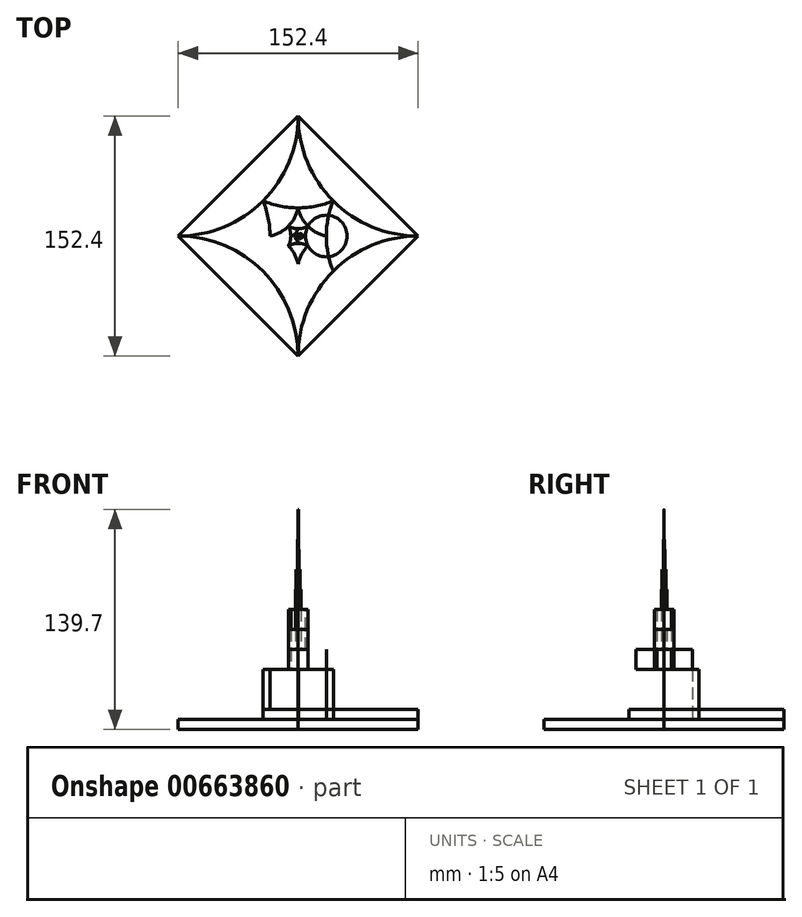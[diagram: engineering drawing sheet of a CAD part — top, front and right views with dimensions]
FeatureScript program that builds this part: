
annotation { "Feature Type Name" : "Feature", "Feature Type Description" : "" }
export const myFeature = defineFeature(function(context is Context, id is Id, definition is map)
    precondition{}
    {
        {
            var Q0;
            Q0=qCreatedBy(makeId("Top.planeOp"),FACE);
            var sketch = newSketch(context, id + "F0", { "sketchPlane" : qUnion([Q0])});
            skLineSegment(sketch, "E0", {"start": v(0, 76.2) * mm, "end": v(-76.2, 0) * mm});
            skLineSegment(sketch, "E1", {"start": v(-76.2, 0) * mm, "end": v(0, -76.2) * mm});
            skLineSegment(sketch, "E2", {"start": v(0, -76.2) * mm, "end": v(76.2, 0) * mm});
            skLineSegment(sketch, "E3", {"start": v(76.2, 0) * mm, "end": v(0, 76.2) * mm});
            skArc(sketch, "E4", {"start": v(-76.2, 0) * mm, "mid": v(-22.32, 22.32) * mm, "end": v(0, 76.2) * mm});
            skArc(sketch, "E5", {"start": v(76.2, 0) * mm, "mid": v(22.35, 22.28) * mm, "end": v(0, 76.1) * mm});
            skArc(sketch, "E6", {"start": v(-76.2, 0) * mm, "mid": v(-22.32, -22.32) * mm, "end": v(0, -76.2) * mm});
            skArc(sketch, "E7", {"start": v(0, -76.2) * mm, "mid": v(22.32, -22.32) * mm, "end": v(76.2, 0) * mm});
            skArc(sketch, "E8", {"start": v(-22.32, 22.32) * mm, "mid": v(0, 17.88) * mm, "end": v(22.32, 22.32) * mm});
            skArc(sketch, "E9", {"start": v(-22.32, -22.32) * mm, "mid": v(0, -17.88) * mm, "end": v(22.32, -22.32) * mm});
            skArc(sketch, "E10", {"start": v(22.32, 22.32) * mm, "mid": v(17.88, 0) * mm, "end": v(22.32, -22.32) * mm});
            skArc(sketch, "E11", {"start": v(-22.32, 22.32) * mm, "mid": v(-17.88, 0) * mm, "end": v(-22.32, -22.32) * mm});
            skArc(sketch, "E12", {"start": v(-17.88, 0) * mm, "mid": v(-6.23, -6.23) * mm, "end": v(0, -17.88) * mm});
            skArc(sketch, "E13", {"start": v(0, -17.88) * mm, "mid": v(6.23, -6.23) * mm, "end": v(17.88, 0) * mm});
            skArc(sketch, "E14", {"start": v(-17.88, 0) * mm, "mid": v(-6.23, 6.23) * mm, "end": v(0, 17.88) * mm});
            skArc(sketch, "E15", {"start": v(0, 17.88) * mm, "mid": v(6.23, 6.23) * mm, "end": v(17.88, 0) * mm});
            skArc(sketch, "E16", {"start": v(-6.23, 6.23) * mm, "mid": v(0, 4.67) * mm, "end": v(6.23, 6.23) * mm});
            skArc(sketch, "E17", {"start": v(-6.23, 6.23) * mm, "mid": v(-4.67, 0) * mm, "end": v(-6.23, -6.23) * mm});
            skArc(sketch, "E18", {"start": v(-6.23, -6.23) * mm, "mid": v(0, -4.67) * mm, "end": v(6.23, -6.23) * mm});
            skArc(sketch, "E19", {"start": v(6.23, 6.23) * mm, "mid": v(4.67, 0) * mm, "end": v(6.23, -6.23) * mm});
            skArc(sketch, "E20", {"start": v(0, 4.67) * mm, "mid": v(1.69, 1.69) * mm, "end": v(4.67, 0) * mm});
            skArc(sketch, "E21", {"start": v(4.67, 0) * mm, "mid": v(1.69, -1.69) * mm, "end": v(0, -4.67) * mm});
            skArc(sketch, "E22", {"start": v(0, -4.67) * mm, "mid": v(-1.69, -1.69) * mm, "end": v(-4.67, 0) * mm});
            skArc(sketch, "E23", {"start": v(0, 4.67) * mm, "mid": v(-1.69, 1.69) * mm, "end": v(-4.67, 0) * mm});
            skArc(sketch, "E24", {"start": v(1.69, 1.69) * mm, "mid": v(0, 1.24) * mm, "end": v(-1.69, 1.69) * mm});
            skArc(sketch, "E25", {"start": v(-1.69, 1.69) * mm, "mid": v(-1.24, 0) * mm, "end": v(-1.69, -1.69) * mm});
            skArc(sketch, "E26", {"start": v(-1.69, -1.69) * mm, "mid": v(0, -1.24) * mm, "end": v(1.69, -1.69) * mm});
            skArc(sketch, "E27", {"start": v(1.69, -1.69) * mm, "mid": v(1.24, 0) * mm, "end": v(1.69, 1.7) * mm});
            skArc(sketch, "E28", {"start": v(0, 1.24) * mm, "mid": v(0.45, 0.45) * mm, "end": v(1.24, 0) * mm});
            skArc(sketch, "E29", {"start": v(1.24, 0) * mm, "mid": v(0.45, -0.45) * mm, "end": v(0, -1.24) * mm});
            skArc(sketch, "E30", {"start": v(0, -1.24) * mm, "mid": v(-0.45, -0.45) * mm, "end": v(-1.24, 0) * mm});
            skArc(sketch, "E31", {"start": v(0, 1.24) * mm, "mid": v(-0.45, 0.45) * mm, "end": v(-1.24, 0) * mm});
            skArc(sketch, "E32", {"start": v(-0.45, 0.45) * mm, "mid": v(0, 0.33) * mm, "end": v(0.45, 0.45) * mm});
            skArc(sketch, "E33", {"start": v(0.45, 0.45) * mm, "mid": v(0.33, 0) * mm, "end": v(0.45, -0.45) * mm});
            skArc(sketch, "E34", {"start": v(0.45, -0.45) * mm, "mid": v(0, -0.33) * mm, "end": v(-0.45, -0.45) * mm});
            skArc(sketch, "E35", {"start": v(-0.45, 0.45) * mm, "mid": v(-0.33, 0) * mm, "end": v(-0.45, -0.45) * mm});
            skArc(sketch, "E36", {"start": v(0, 0.33) * mm, "mid": v(-0.12, 0.12) * mm, "end": v(-0.33, 0) * mm});
            skArc(sketch, "E37", {"start": v(0, 0.33) * mm, "mid": v(0.12, 0.12) * mm, "end": v(0.33, 0) * mm});
            skArc(sketch, "E38", {"start": v(0.33, 0) * mm, "mid": v(0.12, -0.12) * mm, "end": v(0, -0.33) * mm});
            skArc(sketch, "E39", {"start": v(-0.33, 0) * mm, "mid": v(-0.12, -0.12) * mm, "end": v(0, -0.33) * mm});
            skArc(sketch, "E40", {"start": v(0.12, -0.12) * mm, "mid": v(0, -0.09) * mm, "end": v(-0.12, -0.12) * mm});
            skArc(sketch, "E41", {"start": v(-0.12, -0.12) * mm, "mid": v(-0.09, 0) * mm, "end": v(-0.12, 0.12) * mm});
            skArc(sketch, "E42", {"start": v(-0.12, 0.12) * mm, "mid": v(0, 0.09) * mm, "end": v(0.12, 0.12) * mm});
            skArc(sketch, "E43", {"start": v(0.12, 0.12) * mm, "mid": v(0.1, 0) * mm, "end": v(0.12, -0.12) * mm});
            skCircle(sketch, "E44", {"center": v(0, 0) * mm, "radius": 0.09 * mm});
            skSolve(sketch);
        }
        {
            var Q0;
            {var subQ1=sQuery(id+"F0.wireOp",EDGE,"E5");var subQ3=sQuery(id+"F0.wireOp",EDGE,"kofghPFV-T25e-cAOz-wG0u-t3LKG4Hneenn");var subQ4=makeQuery(id+"F0.imprint","INTERSECT",VERTEX,{"derivedFrom":[subQ1,subQ3,sQuery(id+"F0.wireOp",EDGE,"4kuBeRdD-5hCW-bFI1-FARk-7CcU9GoLoFz7")]});Q0=makeQuery(id+"F0.imprint","IMPRINT",FACE,{"disambiguationData":[TD([[makeQuery(id+"F0.imprint","IMPRINT",EDGE,{"disambiguationData":[TD([[subQ4,-1.0]])],"derivedFrom":subQ3}),1.0]])]});}
            var Q1;
            {var subQ0=sQuery(id+"F0.wireOp",EDGE,"E5");var subQ1=sQuery(id+"F0.wireOp",EDGE,"E4");var subQ2=makeQuery(id+"F0.imprint","INTERSECT",VERTEX,{"derivedFrom":[subQ1,subQ0]});Q1=makeQuery(id+"F0.imprint","IMPRINT",FACE,{"disambiguationData":[TD([[makeQuery(id+"F0.imprint","IMPRINT",EDGE,{"disambiguationData":[TD([[subQ2,1.0]])],"derivedFrom":subQ1}),-1.0]])]});}
            var Q2;
            {var subQ3=sQuery(id+"F0.wireOp",EDGE,"0P1LDTDX-IqJU-1oAK-Dlat-AA7q8Yj1gsRT");var subQ6=makeQuery(id+"F0.imprint","INTERSECT",VERTEX,{"derivedFrom":[subQ3,sQuery(id+"F0.wireOp",EDGE,"TcEtzozo-cGTj-XFDn-72LJ-OHSNKTu2x1DY")]});Q2=makeQuery(id+"F0.imprint","IMPRINT",FACE,{"disambiguationData":[TD([[makeQuery(id+"F0.imprint","IMPRINT",EDGE,{"disambiguationData":[TD([[subQ6,1.0]])],"derivedFrom":subQ3}),1.0]])]});}
            var Q3;
            {var subQ1=sQuery(id+"F0.wireOp",EDGE,"E6");var subQ3=sQuery(id+"F0.wireOp",EDGE,"GB3kAdCj-T7ig-4SLS-Dsba-dUtnLU9mhMO3");var subQ4=makeQuery(id+"F0.imprint","INTERSECT",VERTEX,{"derivedFrom":[subQ1,sQuery(id+"F0.wireOp",EDGE,"0P1LDTDX-IqJU-1oAK-Dlat-AA7q8Yj1gsRT"),subQ3]});Q3=makeQuery(id+"F0.imprint","IMPRINT",FACE,{"disambiguationData":[TD([[makeQuery(id+"F0.imprint","IMPRINT",EDGE,{"disambiguationData":[TD([[subQ4,-1.0]])],"derivedFrom":subQ3}),-1.0]])]});}
            var Q4;
            {var subQ1=sQuery(id+"F0.wireOp",EDGE,"E4");var subQ3=sQuery(id+"F0.wireOp",EDGE,"E11");var subQ4=makeQuery(id+"F0.imprint","INTERSECT",VERTEX,{"derivedFrom":[subQ1,sQuery(id+"F0.wireOp",EDGE,"E8"),subQ3]});Q4=makeQuery(id+"F0.imprint","IMPRINT",FACE,{"disambiguationData":[TD([[makeQuery(id+"F0.imprint","IMPRINT",EDGE,{"disambiguationData":[TD([[subQ4,-1.0]])],"derivedFrom":subQ3}),-1.0]])]});}
            var Q5;
            {var subQ3=sQuery(id+"F0.wireOp",EDGE,"E10");var subQ6=makeQuery(id+"F0.imprint","INTERSECT",VERTEX,{"derivedFrom":[subQ3,sQuery(id+"F0.wireOp",EDGE,"E15")]});Q5=makeQuery(id+"F0.imprint","IMPRINT",FACE,{"disambiguationData":[TD([[makeQuery(id+"F0.imprint","IMPRINT",EDGE,{"disambiguationData":[TD([[subQ6,1.0]])],"derivedFrom":subQ3}),1.0]])]});}
            var Q6;
            {var subQ1=sQuery(id+"F0.wireOp",EDGE,"E6");var subQ3=sQuery(id+"F0.wireOp",EDGE,"E9");var subQ4=makeQuery(id+"F0.imprint","INTERSECT",VERTEX,{"derivedFrom":[subQ1,subQ3,sQuery(id+"F0.wireOp",EDGE,"E11")]});Q6=makeQuery(id+"F0.imprint","IMPRINT",FACE,{"disambiguationData":[TD([[makeQuery(id+"F0.imprint","IMPRINT",EDGE,{"disambiguationData":[TD([[subQ4,-1.0]])],"derivedFrom":subQ3}),-1.0]])]});}
            extrude(context, id + "F1", {"entities" : qUnion([Q0, Q1, Q2, Q3, Q4, Q5, Q6]), "depth" : 12.7 * mm, "offsetDistance" : 25.4 * mm, "hasSecondDirection" : true, "secondDirectionOppositeDirection" : false, "secondDirectionDepth" : 6.35 * mm});
        }
        {
            var Q0;
            {var subQ0=sQuery(id+"F0.wireOp",EDGE,"E11");var subQ1=sQuery(id+"F0.wireOp",EDGE,"E8");var subQ2=makeQuery(id+"F0.imprint","INTERSECT",VERTEX,{"derivedFrom":[sQuery(id+"F0.wireOp",EDGE,"E4"),subQ1,subQ0]});Q0=makeQuery(id+"F0.imprint","IMPRINT",FACE,{"disambiguationData":[TD([[makeQuery(id+"F0.imprint","IMPRINT",EDGE,{"disambiguationData":[TD([[subQ2,-1.0]])],"derivedFrom":subQ1}),-1.0]])]});}
            var Q1;
            {var subQ0=sQuery(id+"F0.wireOp",EDGE,"E15");var subQ1=makeQuery(id+"F0.imprint","INTERSECT",VERTEX,{"derivedFrom":[sQuery(id+"F0.wireOp",EDGE,"E13"),subQ0]});Q1=makeQuery(id+"F0.imprint","IMPRINT",FACE,{"disambiguationData":[TD([[makeQuery(id+"F0.imprint","IMPRINT",EDGE,{"disambiguationData":[TD([[subQ1,-1.0]])],"derivedFrom":subQ0}),1.0]])]});}
            var Q2;
            {var subQ0=sQuery(id+"F0.wireOp",EDGE,"E15");var subQ1=sQuery(id+"F0.wireOp",EDGE,"E13");var subQ2=makeQuery(id+"F0.imprint","INTERSECT",VERTEX,{"derivedFrom":[subQ1,subQ0]});Q2=makeQuery(id+"F0.imprint","IMPRINT",FACE,{"disambiguationData":[TD([[makeQuery(id+"F0.imprint","IMPRINT",EDGE,{"disambiguationData":[TD([[subQ2,1.0]])],"derivedFrom":subQ1}),-1.0]])]});}
            var Q3;
            {var subQ0=sQuery(id+"F0.wireOp",EDGE,"E11");var subQ1=sQuery(id+"F0.wireOp",EDGE,"E9");var subQ2=makeQuery(id+"F0.imprint","INTERSECT",VERTEX,{"derivedFrom":[sQuery(id+"F0.wireOp",EDGE,"E6"),subQ1,subQ0]});Q3=makeQuery(id+"F0.imprint","IMPRINT",FACE,{"disambiguationData":[TD([[makeQuery(id+"F0.imprint","IMPRINT",EDGE,{"disambiguationData":[TD([[subQ2,-1.0]])],"derivedFrom":subQ1}),1.0]])]});}
            extrude(context, id + "F2", {"entities" : qUnion([Q0, Q1, Q2, Q3]), "depth" : 38.1 * mm, "offsetDistance" : 25.4 * mm, "hasSecondDirection" : true, "secondDirectionOppositeDirection" : false, "secondDirectionDepth" : 12.7 * mm});
        }
        {
            var Q0;
            {var subQ0=sQuery(id+"F0.wireOp",EDGE,"E15");var subQ1=sQuery(id+"F0.wireOp",EDGE,"E14");var subQ2=makeQuery(id+"F0.imprint","INTERSECT",VERTEX,{"derivedFrom":[sQuery(id+"F0.wireOp",EDGE,"E8"),subQ1,subQ0]});Q0=makeQuery(id+"F0.imprint","IMPRINT",FACE,{"disambiguationData":[TD([[makeQuery(id+"F0.imprint","IMPRINT",EDGE,{"disambiguationData":[TD([[subQ2,1.0]])],"derivedFrom":subQ1}),-1.0]])]});}
            var Q1;
            {var subQ1=sQuery(id+"F0.wireOp",EDGE,"E15");var subQ8=sQuery(id+"F0.wireOp",EDGE,"E13");var subQ9=makeQuery(id+"F0.imprint","INTERSECT",VERTEX,{"derivedFrom":[subQ8,subQ1]});Q1=makeQuery(id+"F0.imprint","IMPRINT",FACE,{"disambiguationData":[TD([[makeQuery(id+"F0.imprint","IMPRINT",EDGE,{"disambiguationData":[TD([[subQ9,1.0]])],"derivedFrom":subQ8}),1.0]])]});}
            var Q2;
            {var subQ3=sQuery(id+"F0.wireOp",EDGE,"E17");var subQ6=makeQuery(id+"F0.imprint","INTERSECT",VERTEX,{"derivedFrom":[subQ3,sQuery(id+"F0.wireOp",EDGE,"E22")]});Q2=makeQuery(id+"F0.imprint","IMPRINT",FACE,{"disambiguationData":[TD([[makeQuery(id+"F0.imprint","IMPRINT",EDGE,{"disambiguationData":[TD([[subQ6,1.0]])],"derivedFrom":subQ3}),-1.0]])]});}
            var Q3;
            {var subQ0=sQuery(id+"F0.wireOp",EDGE,"E19");var subQ1=sQuery(id+"F0.wireOp",EDGE,"E18");var subQ2=makeQuery(id+"F0.imprint","INTERSECT",VERTEX,{"derivedFrom":[subQ1,subQ0]});Q3=makeQuery(id+"F0.imprint","IMPRINT",FACE,{"disambiguationData":[TD([[makeQuery(id+"F0.imprint","IMPRINT",EDGE,{"disambiguationData":[TD([[subQ2,-1.0]])],"derivedFrom":subQ0}),-1.0]])]});}
            extrude(context, id + "F3", {"entities" : qUnion([Q0, Q1, Q2, Q3]), "depth" : 50.8 * mm, "offsetDistance" : 25.4 * mm, "hasSecondDirection" : true, "secondDirectionOppositeDirection" : false, "secondDirectionDepth" : 38.1 * mm});
        }
        {
            var Q0;
            {var subQ0=sQuery(id+"F0.wireOp",EDGE,"E22");var subQ4=sQuery(id+"F0.wireOp",EDGE,"E17");var subQ7=makeQuery(id+"F0.imprint","INTERSECT",VERTEX,{"derivedFrom":[subQ4,subQ0]});Q0=makeQuery(id+"F0.imprint","IMPRINT",FACE,{"disambiguationData":[TD([[makeQuery(id+"F0.imprint","IMPRINT",EDGE,{"disambiguationData":[TD([[subQ7,1.0]])],"derivedFrom":subQ0}),1.0]])]});}
            var Q1;
            {var subQ0=sQuery(id+"F0.wireOp",EDGE,"E19");var subQ1=sQuery(id+"F0.wireOp",EDGE,"E18");var subQ2=makeQuery(id+"F0.imprint","INTERSECT",VERTEX,{"derivedFrom":[subQ1,subQ0]});Q1=makeQuery(id+"F0.imprint","IMPRINT",FACE,{"disambiguationData":[TD([[makeQuery(id+"F0.imprint","IMPRINT",EDGE,{"disambiguationData":[TD([[subQ2,1.0]])],"derivedFrom":subQ0}),-1.0]])]});}
            var Q2;
            {var subQ0=sQuery(id+"F0.wireOp",EDGE,"E20");var subQ3=makeQuery(id+"F0.imprint","INTERSECT",VERTEX,{"derivedFrom":[subQ0,sQuery(id+"F0.wireOp",EDGE,"E24")]});Q2=makeQuery(id+"F0.imprint","IMPRINT",FACE,{"disambiguationData":[TD([[makeQuery(id+"F0.imprint","IMPRINT",EDGE,{"disambiguationData":[TD([[subQ3,-1.0]])],"derivedFrom":subQ0}),1.0]])]});}
            var Q3;
            {var subQ3=sQuery(id+"F0.wireOp",EDGE,"E23");Q3=makeQuery(id+"F0.imprint","IMPRINT",FACE,{"disambiguationData":[TD([[makeQuery(id+"F0.imprint","IMPRINT",EDGE,{"derivedFrom":subQ3}),-1.0]])]});}
            extrude(context, id + "F4", {"entities" : qUnion([Q0, Q1, Q2, Q3]), "depth" : 63.5 * mm, "offsetDistance" : 25.4 * mm, "hasSecondDirection" : true, "secondDirectionOppositeDirection" : false, "secondDirectionDepth" : 50.8 * mm});
        }
        {
            var Q0;
            {var subQ3=sQuery(id+"F0.wireOp",EDGE,"E19");var subQ6=sQuery(id+"F0.wireOp",EDGE,"E20");var subQ8=makeQuery(id+"F0.imprint","INTERSECT",VERTEX,{"derivedFrom":[subQ3,subQ6]});Q0=makeQuery(id+"F0.imprint","IMPRINT",FACE,{"disambiguationData":[TD([[makeQuery(id+"F0.imprint","IMPRINT",EDGE,{"disambiguationData":[TD([[subQ8,-1.0]])],"derivedFrom":subQ3}),-1.0]])]});}
            var Q1;
            {var subQ0=sQuery(id+"F0.wireOp",EDGE,"E22");var subQ1=sQuery(id+"F0.wireOp",EDGE,"E21");var subQ2=makeQuery(id+"F0.imprint","INTERSECT",VERTEX,{"derivedFrom":[sQuery(id+"F0.wireOp",EDGE,"E18"),subQ1,subQ0]});Q1=makeQuery(id+"F0.imprint","IMPRINT",FACE,{"disambiguationData":[TD([[makeQuery(id+"F0.imprint","IMPRINT",EDGE,{"disambiguationData":[TD([[subQ2,1.0]])],"derivedFrom":subQ1}),-1.0]])]});}
            var Q2;
            {var subQ4=sQuery(id+"F0.wireOp",EDGE,"E23");Q2=makeQuery(id+"F0.imprint","IMPRINT",FACE,{"disambiguationData":[TD([[makeQuery(id+"F0.imprint","IMPRINT",EDGE,{"derivedFrom":subQ4}),1.0]])]});}
            extrude(context, id + "F5", {"entities" : qUnion([Q0, Q1, Q2]), "depth" : 76.2 * mm, "offsetDistance" : 25.4 * mm, "hasSecondDirection" : true, "secondDirectionOppositeDirection" : false, "secondDirectionDepth" : 63.5 * mm});
        }
        {
            var Q0;
            {var subQ1=sQuery(id+"F0.wireOp",EDGE,"E24");var subQ4=sQuery(id+"F0.wireOp",EDGE,"E25");var subQ5=makeQuery(id+"F0.imprint","INTERSECT",VERTEX,{"derivedFrom":[subQ1,subQ4]});Q0=makeQuery(id+"F0.imprint","IMPRINT",FACE,{"disambiguationData":[TD([[makeQuery(id+"F0.imprint","IMPRINT",EDGE,{"disambiguationData":[TD([[subQ5,-1.0]])],"derivedFrom":subQ4}),1.0]])]});}
            var Q1;
            {var subQ1=sQuery(id+"F0.wireOp",EDGE,"E24");var subQ6=sQuery(id+"F0.wireOp",EDGE,"E20");var subQ8=makeQuery(id+"F0.imprint","INTERSECT",VERTEX,{"derivedFrom":[subQ6,subQ1]});Q1=makeQuery(id+"F0.imprint","IMPRINT",FACE,{"disambiguationData":[TD([[makeQuery(id+"F0.imprint","IMPRINT",EDGE,{"disambiguationData":[TD([[subQ8,-1.0]])],"derivedFrom":subQ6}),-1.0]])]});}
            var Q2;
            {var subQ3=sQuery(id+"F0.wireOp",EDGE,"E34");var subQ5=sQuery(id+"F0.wireOp",EDGE,"E33");var subQ6=makeQuery(id+"F0.imprint","INTERSECT",VERTEX,{"derivedFrom":[subQ5,subQ3]});Q2=makeQuery(id+"F0.imprint","IMPRINT",FACE,{"disambiguationData":[TD([[makeQuery(id+"F0.imprint","IMPRINT",EDGE,{"disambiguationData":[TD([[subQ6,1.0]])],"derivedFrom":subQ5}),1.0]])]});}
            var Q3;
            {var subQ0=sQuery(id+"F0.wireOp",EDGE,"E30");var subQ1=makeQuery(id+"F0.imprint","INTERSECT",VERTEX,{"derivedFrom":[subQ0,sQuery(id+"F0.wireOp",EDGE,"E34")]});Q3=makeQuery(id+"F0.imprint","IMPRINT",FACE,{"disambiguationData":[TD([[makeQuery(id+"F0.imprint","IMPRINT",EDGE,{"disambiguationData":[TD([[subQ1,-1.0]])],"derivedFrom":subQ0}),1.0]])]});}
            extrude(context, id + "F6", {"entities" : qUnion([Q0, Q1, Q2, Q3]), "depth" : 88.9 * mm, "offsetDistance" : 25.4 * mm, "hasSecondDirection" : true, "secondDirectionOppositeDirection" : false, "secondDirectionDepth" : 76.2 * mm});
        }
        {
            var Q0;
            {var subQ0=sQuery(id+"F0.wireOp",EDGE,"E31");var subQ1=sQuery(id+"F0.wireOp",EDGE,"E28");var subQ2=makeQuery(id+"F0.imprint","INTERSECT",VERTEX,{"derivedFrom":[sQuery(id+"F0.wireOp",EDGE,"E24"),subQ1,subQ0]});Q0=makeQuery(id+"F0.imprint","IMPRINT",FACE,{"disambiguationData":[TD([[makeQuery(id+"F0.imprint","IMPRINT",EDGE,{"disambiguationData":[TD([[subQ2,-1.0]])],"derivedFrom":subQ1}),-1.0]])]});}
            var Q1;
            {var subQ0=sQuery(id+"F0.wireOp",EDGE,"E31");var subQ1=sQuery(id+"F0.wireOp",EDGE,"E30");var subQ2=makeQuery(id+"F0.imprint","INTERSECT",VERTEX,{"derivedFrom":[subQ1,subQ0]});Q1=makeQuery(id+"F0.imprint","IMPRINT",FACE,{"disambiguationData":[TD([[makeQuery(id+"F0.imprint","IMPRINT",EDGE,{"disambiguationData":[TD([[subQ2,1.0]])],"derivedFrom":subQ1}),-1.0]])]});}
            var Q2;
            {var subQ0=sQuery(id+"F0.wireOp",EDGE,"E29");var subQ3=sQuery(id+"F0.wireOp",EDGE,"E33");var subQ5=makeQuery(id+"F0.imprint","INTERSECT",VERTEX,{"derivedFrom":[subQ0,subQ3]});Q2=makeQuery(id+"F0.imprint","IMPRINT",FACE,{"disambiguationData":[TD([[makeQuery(id+"F0.imprint","IMPRINT",EDGE,{"disambiguationData":[TD([[subQ5,1.0]])],"derivedFrom":subQ0}),-1.0]])]});}
            var Q3;
            {var subQ3=sQuery(id+"F0.wireOp",EDGE,"E34");var subQ6=makeQuery(id+"F0.imprint","INTERSECT",VERTEX,{"derivedFrom":[subQ3,sQuery(id+"F0.wireOp",EDGE,"E38")]});Q3=makeQuery(id+"F0.imprint","IMPRINT",FACE,{"disambiguationData":[TD([[makeQuery(id+"F0.imprint","IMPRINT",EDGE,{"disambiguationData":[TD([[subQ6,1.0]])],"derivedFrom":subQ3}),1.0]])]});}
            extrude(context, id + "F7", {"entities" : qUnion([Q0, Q1, Q2, Q3]), "depth" : 101.6 * mm, "offsetDistance" : 25.4 * mm, "hasSecondDirection" : true, "secondDirectionOppositeDirection" : false, "secondDirectionDepth" : 88.9 * mm});
        }
        {
            var Q0;
            {var subQ0=sQuery(id+"F0.wireOp",EDGE,"E33");var subQ1=sQuery(id+"F0.wireOp",EDGE,"E32");var subQ2=makeQuery(id+"F0.imprint","INTERSECT",VERTEX,{"derivedFrom":[sQuery(id+"F0.wireOp",EDGE,"E28"),subQ1,subQ0]});Q0=makeQuery(id+"F0.imprint","IMPRINT",FACE,{"disambiguationData":[TD([[makeQuery(id+"F0.imprint","IMPRINT",EDGE,{"disambiguationData":[TD([[subQ2,1.0]])],"derivedFrom":subQ1}),-1.0]])]});}
            var Q1;
            {var subQ0=sQuery(id+"F0.wireOp",EDGE,"E35");var subQ1=sQuery(id+"F0.wireOp",EDGE,"E32");var subQ2=makeQuery(id+"F0.imprint","INTERSECT",VERTEX,{"derivedFrom":[sQuery(id+"F0.wireOp",EDGE,"E31"),subQ1,subQ0]});Q1=makeQuery(id+"F0.imprint","IMPRINT",FACE,{"disambiguationData":[TD([[makeQuery(id+"F0.imprint","IMPRINT",EDGE,{"disambiguationData":[TD([[subQ2,-1.0]])],"derivedFrom":subQ1}),-1.0]])]});}
            var Q2;
            {var subQ1=sQuery(id+"F0.wireOp",EDGE,"E33");var subQ4=sQuery(id+"F0.wireOp",EDGE,"E29");var subQ5=makeQuery(id+"F0.imprint","INTERSECT",VERTEX,{"derivedFrom":[subQ4,subQ1]});Q2=makeQuery(id+"F0.imprint","IMPRINT",FACE,{"disambiguationData":[TD([[makeQuery(id+"F0.imprint","IMPRINT",EDGE,{"disambiguationData":[TD([[subQ5,-1.0]])],"derivedFrom":subQ4}),-1.0]])]});}
            var Q3;
            {var subQ1=sQuery(id+"F0.wireOp",EDGE,"E30");var subQ6=sQuery(id+"F0.wireOp",EDGE,"E34");var subQ9=makeQuery(id+"F0.imprint","INTERSECT",VERTEX,{"derivedFrom":[subQ1,subQ6]});Q3=makeQuery(id+"F0.imprint","IMPRINT",FACE,{"disambiguationData":[TD([[makeQuery(id+"F0.imprint","IMPRINT",EDGE,{"disambiguationData":[TD([[subQ9,-1.0]])],"derivedFrom":subQ1}),-1.0]])]});}
            extrude(context, id + "F8", {"entities" : qUnion([Q0, Q1, Q2, Q3]), "depth" : 114.3 * mm, "offsetDistance" : 25.4 * mm, "hasSecondDirection" : true, "secondDirectionOppositeDirection" : false, "secondDirectionDepth" : 101.6 * mm});
        }
        {
            var Q0;
            {var subQ3=sQuery(id+"F0.wireOp",EDGE,"E43");Q0=makeQuery(id+"F0.imprint","IMPRINT",FACE,{"disambiguationData":[TD([[makeQuery(id+"F0.imprint","IMPRINT",EDGE,{"derivedFrom":subQ3}),1.0]])]});}
            var Q1;
            {var subQ3=sQuery(id+"F0.wireOp",EDGE,"E42");Q1=makeQuery(id+"F0.imprint","IMPRINT",FACE,{"disambiguationData":[TD([[makeQuery(id+"F0.imprint","IMPRINT",EDGE,{"derivedFrom":subQ3}),1.0]])]});}
            var Q2;
            {var subQ3=sQuery(id+"F0.wireOp",EDGE,"E41");Q2=makeQuery(id+"F0.imprint","IMPRINT",FACE,{"disambiguationData":[TD([[makeQuery(id+"F0.imprint","IMPRINT",EDGE,{"derivedFrom":subQ3}),1.0]])]});}
            var Q3;
            {var subQ3=sQuery(id+"F0.wireOp",EDGE,"E40");Q3=makeQuery(id+"F0.imprint","IMPRINT",FACE,{"disambiguationData":[TD([[makeQuery(id+"F0.imprint","IMPRINT",EDGE,{"derivedFrom":subQ3}),1.0]])]});}
            extrude(context, id + "F9", {"entities" : qUnion([Q0, Q1, Q2, Q3]), "depth" : 120.65 * mm, "offsetDistance" : 25.4 * mm, "hasSecondDirection" : true, "secondDirectionOppositeDirection" : false, "secondDirectionDepth" : 114.3 * mm});
        }
        {
            var Q0;
            Q0=makeQuery(id+"F0.imprint","IMPRINT",FACE,{"disambiguationData":[TD([[makeQuery(id+"F0.imprint","IMPRINT",EDGE,{"derivedFrom":sQuery(id+"F0.wireOp",EDGE,"E44")}),1.0]])]});
            extrude(context, id + "F10", {"entities" : qUnion([Q0]), "depth" : 139.7 * mm, "offsetDistance" : 25.4 * mm});
        }
        {
            var Q0;
            {var subQ0=sQuery(id+"F0.wireOp",EDGE,"E1");Q0=makeQuery(id+"F0.imprint","IMPRINT",FACE,{"disambiguationData":[TD([[makeQuery(id+"F0.imprint","IMPRINT",EDGE,{"derivedFrom":subQ0}),1.0]])]});}
            var Q1;
            {var subQ0=sQuery(id+"F0.wireOp",EDGE,"E2");Q1=makeQuery(id+"F0.imprint","IMPRINT",FACE,{"disambiguationData":[TD([[makeQuery(id+"F0.imprint","IMPRINT",EDGE,{"derivedFrom":subQ0}),1.0]])]});}
            var Q2;
            {var subQ0=sQuery(id+"F0.wireOp",EDGE,"E3");Q2=makeQuery(id+"F0.imprint","IMPRINT",FACE,{"disambiguationData":[TD([[makeQuery(id+"F0.imprint","IMPRINT",EDGE,{"derivedFrom":subQ0}),1.0]])]});}
            var Q3;
            {var subQ0=sQuery(id+"F0.wireOp",EDGE,"E0");Q3=makeQuery(id+"F0.imprint","IMPRINT",FACE,{"disambiguationData":[TD([[makeQuery(id+"F0.imprint","IMPRINT",EDGE,{"derivedFrom":subQ0}),1.0]])]});}
            extrude(context, id + "F11", {"entities" : qUnion([Q0, Q1, Q2, Q3]), "depth" : 6.35 * mm, "offsetDistance" : 25.4 * mm});
        }
    });
